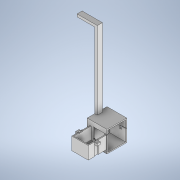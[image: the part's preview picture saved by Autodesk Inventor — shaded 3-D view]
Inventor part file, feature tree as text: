
AUTODESK INVENTOR PART (.ipt)
format: ipt  version: 2020.2 (Build 242310000, 310)  size: 563,712 bytes
history: native  units: mm
features: sketch x25, extrude x24, projected_geometry x8, hole x1
ambient origin geometry x8: Origin, YZ Plane, XZ Plane, XY Plane, X Axis, Y Axis, Z Axis, Center Point
bodies: Solid1 (feature_tree)
feature tree (58):
  sketch  "Sketch1"  dims[d0=29.0mm d1=35.0mm]
  extrude  "Extrusion1"  Depth=35.0mm
  extrude  "Extrusion2"  Depth=2.0mm
  extrude  "Extrusion3"  Depth=39.0mm
  hole  "Hole1"  [1 undecoded]
  extrude  "Extrusion4"  Depth=10.0mm
  sketch  "Sketch5"  dims[d10=10.0mm d11=0.0mm d12=4.2mm]
  sketch  "Sketch6"  dims[d13=4.475mm d14=26.05mm]
  extrude  "Extrusion5"  Depth=26.05mm
  extrude  "Extrusion6"  Depth=39.0mm
  extrude  "Extrusion7"  Depth=33.0mm TaperAngle=0.0deg
  sketch  "Sketch10"  dims[d27=7.0mm d28=7.0mm]
  extrude  "Extrusion8"  Depth=7.0mm
  extrude  "Extrusion9"  Depth=7.0mm
  extrude  "Extrusion14"  Depth=10.0mm
  extrude  "Extrusion15"  Depth=20.0mm
  extrude  "Extrusion16"  Depth=22.5mm
  extrude  "Extrusion17"  Depth=1.0mm
  extrude  "Extrusion18"  Depth=24.0mm
  extrude  "Extrusion19"  Depth=1.0mm
  extrude  "Extrusion25"  Depth=26.0mm
  extrude  "Extrusion26"  Depth=1.0mm
  extrude  "Extrusion27"  Depth=1.0mm
  extrude  "Extrusion21"  Depth=26.0mm TaperAngle=0.0deg
  extrude  "Extrusion22"  Depth=1.0mm TaperAngle=0.0deg
  extrude  "Extrusion23"  Depth=14.0mm
  extrude  "Extrusion24"  TaperAngle=90.0deg  [1 undecoded]
  extrude  "Extrusion28"  Depth=3.5mm
  extrude  "Extrusion29"  Depth=7.0mm
  sketch  "Sketch2"  dims[d2=2.0mm d3=2.0mm]
  sketch  "Sketch3"  dims[d4=33.0mm d5=39.0mm]
  sketch  "Sketch4"  dims[d6=2.0mm d7=0.0mm d8=40.0mm d9=0.0mm]
  sketch  "Sketch7"  dims[d15=29.6mm]
  projected_geometry  "Projected Loop1"
  sketch  "Sketch8"  dims[d16=3.4mm d17=6.0mm d18=6.3mm d19=2.0mm d20=90.0deg d21=8.0mm d22=20.594885mm d23=39.0mm]
  sketch  "Sketch9"  dims[d24=2.0mm d25=33.0mm d26=0.0mm]
  sketch  "Sketch11"  dims[d29=7.0mm d30=7.0mm]
  sketch  "Sketch16"  dims[d31=5.0mm d32=0.0mm d33=10.0mm]
  sketch  "Sketch17"  dims[d34=3.5mm d35=20.0mm]
  sketch  "Sketch18"  dims[d36=90.0deg d37=22.5mm]
  projected_geometry  "Projected Loop4"
  sketch  "Sketch19"  dims[d38=10.0mm d39=0.0mm d40=1.0mm]
  projected_geometry  "Projected Loop5"
  sketch  "Sketch21"  dims[d41=10.0mm d42=0.0mm d43=24.0mm]
  projected_geometry  "Projected Loop6"
  sketch  "Sketch25"  dims[d44=30.48mm d45=1.0mm]
  sketch  "Sketch26"  dims[d46=31.48mm d47=26.0mm]
  sketch  "Sketch27"  dims[d48=34.0mm d49=0.0mm d50=1.0mm]
  sketch  "Sketch28"  dims[d51=29.48mm d52=0.0mm d69=1.0mm]
  sketch  "Sketch30"  dims[d70=35.0mm d71=26.0mm d72=0.0mm]
  projected_geometry  "Projected Loop7"
  sketch  "Sketch31"  dims[d73=10.0mm d74=0.0mm d75=1.0mm d76=0.0mm]
  projected_geometry  "Projected Loop8"
  sketch  "Sketch32"  dims[d77=1.0mm d78=0.0mm d79=14.0mm]
  projected_geometry  "Projected Loop9"
  projected_geometry  "Projected Loop10"
  sketch  "Sketch34"  dims[d80=17.5mm d81=90.0deg]
  sketch  "Sketch35"  dims[d82=35.0mm d83=3.5mm d84=7.0mm d85=7.0mm d86=7.0mm d87=3.4mm d88=3.4mm d89=5.0mm d90=0.0mm d91=1.0mm d92=0.0mm d118=15.0mm d119=10.0mm d120=5.0mm d121=12.7mm d122=0.0mm d123=5.0mm d124=35.0mm d125=0.0mm d126=152.9042mm d127=0.0mm d128=5.0mm d129=35.0mm d130=0.0mm d131=1.0mm d132=0.0mm d133=1.0mm d134=0.0mm d135=1.0mm d136=0.0mm d137=1.0mm d138=0.0mm d139=16.0mm d140=10.0mm d141=1.5mm d142=2.0mm d143=5.0mm d144=3.5mm d145=5.5mm d146=10.0mm d147=0.0mm d54=0.5mm d55=0.872665mm d56=0.5mm d57=0.872665mm d58=0.5mm d59=0.872665mm d60=0.5mm d61=0.872665mm d116=0.5mm d117=0.872665mm]
note: 2 required parameter values undecoded (feature->parameter linkage not recoverable at this tier; creation-order binding heuristic only, values carry confidence <= 0.55)
